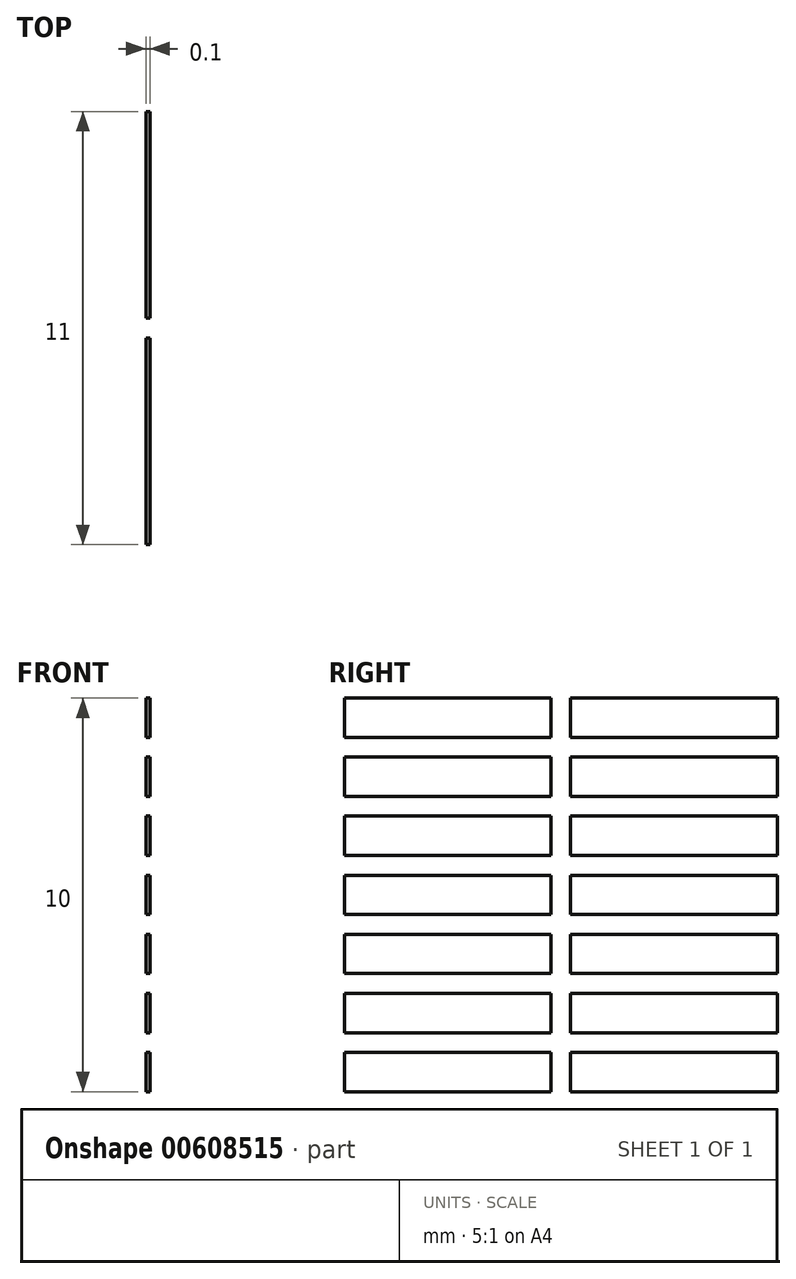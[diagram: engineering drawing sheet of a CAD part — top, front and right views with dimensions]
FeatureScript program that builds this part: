
annotation { "Feature Type Name" : "Feature", "Feature Type Description" : "" }
export const myFeature = defineFeature(function(context is Context, id is Id, definition is map)
    precondition{}
    {
        {
            var Q0;
            Q0=qCreatedBy(makeId("Right.planeOp"),FACE);
            var sketch = newSketch(context, id + "F0", { "sketchPlane" : qUnion([Q0])});
            skPoint(sketch, "E0.0", {"position": v(0, 0) * mm});
            skLineSegment(sketch, "E1.bottom", {"start": v(0, 0) * mm, "end": v(11.5, 0) * mm});
            skLineSegment(sketch, "E1.top", {"start": v(0, -11.5) * mm, "end": v(11.5, -11.5) * mm});
            skLineSegment(sketch, "E1.left", {"start": v(0, 0) * mm, "end": v(0, -11.5) * mm});
            skLineSegment(sketch, "E1.right", {"start": v(11.5, 0) * mm, "end": v(11.5, -11.5) * mm});
            skLineSegment(sketch, "E2.0", {"start": v(11.25, -0.25) * mm, "end": v(11.25, -1.25) * mm});
            skLineSegment(sketch, "E2.1", {"start": v(0.25, -0.25) * mm, "end": v(5.5, -0.25) * mm});
            skLineSegment(sketch, "E2.2", {"start": v(0.25, -0.25) * mm, "end": v(0.25, -1.25) * mm});
            skLineSegment(sketch, "E3.0", {"start": v(0.25, -10.25) * mm, "end": v(5.5, -10.25) * mm});
            skLineSegment(sketch, "E4", {"start": v(0.25, -1.25) * mm, "end": v(5.5, -1.25) * mm});
            skLineSegment(sketch, "E5", {"start": v(5.5, -1.25) * mm, "end": v(5.5, -0.25) * mm});
            skLineSegment(sketch, "E6.0", {"start": v(0.25, -1.75) * mm, "end": v(5.5, -1.75) * mm});
            skLineSegment(sketch, "E7", {"start": v(5.5, -1.75) * mm, "end": v(5.5, -2.75) * mm});
            skLineSegment(sketch, "E8", {"start": v(5.5, -2.75) * mm, "end": v(0.25, -2.75) * mm});
            skLineSegment(sketch, "E9.0", {"start": v(5.5, -3.25) * mm, "end": v(0.25, -3.25) * mm});
            skLineSegment(sketch, "E10", {"start": v(5.5, -3.25) * mm, "end": v(5.5, -4.25) * mm});
            skLineSegment(sketch, "E11", {"start": v(5.5, -4.25) * mm, "end": v(0.25, -4.25) * mm});
            skLineSegment(sketch, "E12.0", {"start": v(5.5, -4.75) * mm, "end": v(0.25, -4.75) * mm});
            skLineSegment(sketch, "E13", {"start": v(5.5, -4.75) * mm, "end": v(5.5, -5.75) * mm});
            skLineSegment(sketch, "E14", {"start": v(5.5, -5.75) * mm, "end": v(0.25, -5.75) * mm});
            skLineSegment(sketch, "E15.0", {"start": v(5.5, -6.25) * mm, "end": v(0.25, -6.25) * mm});
            skLineSegment(sketch, "E16", {"start": v(5.5, -6.25) * mm, "end": v(5.5, -7.25) * mm});
            skLineSegment(sketch, "E17", {"start": v(5.5, -7.25) * mm, "end": v(0.25, -7.25) * mm});
            skLineSegment(sketch, "E18.0", {"start": v(5.5, -7.75) * mm, "end": v(0.25, -7.75) * mm});
            skLineSegment(sketch, "E19", {"start": v(5.5, -7.75) * mm, "end": v(5.5, -8.75) * mm});
            skLineSegment(sketch, "E20", {"start": v(5.5, -8.75) * mm, "end": v(0.25, -8.75) * mm});
            skLineSegment(sketch, "E21.0", {"start": v(5.5, -9.25) * mm, "end": v(0.25, -9.25) * mm});
            skLineSegment(sketch, "E22", {"start": v(5.5, -9.25) * mm, "end": v(5.5, -10.25) * mm});
            skPoint(sketch, "E23.MirrorP", {"position": v(11.5, 0) * mm});
            skLineSegment(sketch, "E24.MirrorCS", {"start": v(6, -9.25) * mm, "end": v(11.25, -9.25) * mm});
            skLineSegment(sketch, "E25.MirrorCS", {"start": v(6, -4.75) * mm, "end": v(6, -5.75) * mm});
            skLineSegment(sketch, "E26.MirrorCS", {"start": v(6, -7.25) * mm, "end": v(11.25, -7.25) * mm});
            skLineSegment(sketch, "E27.MirrorCS", {"start": v(6, -8.75) * mm, "end": v(11.25, -8.75) * mm});
            skLineSegment(sketch, "E28.MirrorCS", {"start": v(6, -5.75) * mm, "end": v(11.25, -5.75) * mm});
            skLineSegment(sketch, "E29.MirrorCS", {"start": v(6, -4.25) * mm, "end": v(11.25, -4.25) * mm});
            skLineSegment(sketch, "E30.MirrorCS", {"start": v(6, -6.25) * mm, "end": v(11.25, -6.25) * mm});
            skLineSegment(sketch, "E31.MirrorCS", {"start": v(6, -2.75) * mm, "end": v(11.25, -2.75) * mm});
            skLineSegment(sketch, "E32.MirrorCS", {"start": v(6, -3.25) * mm, "end": v(11.25, -3.25) * mm});
            skLineSegment(sketch, "E33.MirrorCS", {"start": v(6, -7.75) * mm, "end": v(11.25, -7.75) * mm});
            skLineSegment(sketch, "E34.MirrorCS", {"start": v(6, -9.25) * mm, "end": v(6, -10.25) * mm});
            skLineSegment(sketch, "E35.MirrorCS", {"start": v(6, -1.75) * mm, "end": v(6, -2.75) * mm});
            skLineSegment(sketch, "E36.MirrorCS", {"start": v(11.25, -1.75) * mm, "end": v(6, -1.75) * mm});
            skLineSegment(sketch, "E37.MirrorCS", {"start": v(6, -3.25) * mm, "end": v(6, -4.25) * mm});
            skLineSegment(sketch, "E38.MirrorCS", {"start": v(6, -1.25) * mm, "end": v(6, -0.25) * mm});
            skLineSegment(sketch, "E39.MirrorCS", {"start": v(11.25, -1.25) * mm, "end": v(6, -1.25) * mm});
            skLineSegment(sketch, "E40.MirrorCS", {"start": v(6, -7.75) * mm, "end": v(6, -8.75) * mm});
            skLineSegment(sketch, "E41.MirrorCS", {"start": v(6, -6.25) * mm, "end": v(6, -7.25) * mm});
            skLineSegment(sketch, "E42.MirrorCS", {"start": v(6, -4.75) * mm, "end": v(11.25, -4.75) * mm});
            skPoint(sketch, "E43.orphan", {"position": v(11.5, -10.25) * mm});
            skLineSegment(sketch, "E44.trimOffspring", {"start": v(6, -10.25) * mm, "end": v(11.25, -10.25) * mm});
            skPoint(sketch, "E45.orphan", {"position": v(0, -10.25) * mm});
            skLineSegment(sketch, "E46.trimOffspring", {"start": v(0.25, -9.25) * mm, "end": v(0.25, -10.25) * mm});
            skLineSegment(sketch, "E47.trimOffspring", {"start": v(11.25, -9.25) * mm, "end": v(11.25, -10.25) * mm});
            skLineSegment(sketch, "E48.trimOffspring", {"start": v(11.25, -7.75) * mm, "end": v(11.25, -8.75) * mm});
            skLineSegment(sketch, "E49.trimOffspring", {"start": v(0.25, -7.75) * mm, "end": v(0.25, -8.75) * mm});
            skLineSegment(sketch, "E50.trimOffspring", {"start": v(11.25, -6.25) * mm, "end": v(11.25, -7.25) * mm});
            skLineSegment(sketch, "E51.trimOffspring", {"start": v(11.25, -4.75) * mm, "end": v(11.25, -5.75) * mm});
            skLineSegment(sketch, "E52.trimOffspring", {"start": v(0.25, -6.25) * mm, "end": v(0.25, -7.25) * mm});
            skLineSegment(sketch, "E53.trimOffspring", {"start": v(0.25, -4.75) * mm, "end": v(0.25, -5.75) * mm});
            skLineSegment(sketch, "E54.trimOffspring", {"start": v(0.25, -3.25) * mm, "end": v(0.25, -4.25) * mm});
            skLineSegment(sketch, "E55.trimOffspring", {"start": v(0.25, -1.75) * mm, "end": v(0.25, -2.75) * mm});
            skLineSegment(sketch, "E56.trimOffspring", {"start": v(11.25, -3.25) * mm, "end": v(11.25, -4.25) * mm});
            skLineSegment(sketch, "E57.trimOffspring", {"start": v(11.25, -1.75) * mm, "end": v(11.25, -2.75) * mm});
            skLineSegment(sketch, "E58.trimOffspring", {"start": v(6, -0.25) * mm, "end": v(11.25, -0.25) * mm});
            skSolve(sketch);
        }
        {
            var Q0;
            Q0=makeQuery(id+"F0.imprint","IMPRINT",FACE,{"disambiguationData":[TD([[makeQuery(id+"F0.imprint","IMPRINT",EDGE,{"derivedFrom":sQuery(id+"F0.wireOp",EDGE,"E18.0")}),1.0]])]});
            var Q1;
            Q1=makeQuery(id+"F0.imprint","IMPRINT",FACE,{"disambiguationData":[TD([[makeQuery(id+"F0.imprint","IMPRINT",EDGE,{"derivedFrom":sQuery(id+"F0.wireOp",EDGE,"E3.0")}),1.0]])]});
            var Q2;
            Q2=makeQuery(id+"F0.imprint","IMPRINT",FACE,{"disambiguationData":[TD([[makeQuery(id+"F0.imprint","IMPRINT",EDGE,{"derivedFrom":sQuery(id+"F0.wireOp",EDGE,"E29.MirrorCS")}),1.0]])]});
            var Q3;
            Q3=makeQuery(id+"F0.imprint","IMPRINT",FACE,{"disambiguationData":[TD([[makeQuery(id+"F0.imprint","IMPRINT",EDGE,{"derivedFrom":sQuery(id+"F0.wireOp",EDGE,"E6.0")}),-1.0]])]});
            var Q4;
            Q4=makeQuery(id+"F0.imprint","IMPRINT",FACE,{"disambiguationData":[TD([[makeQuery(id+"F0.imprint","IMPRINT",EDGE,{"derivedFrom":sQuery(id+"F0.wireOp",EDGE,"E31.MirrorCS")}),1.0]])]});
            var Q5;
            Q5=makeQuery(id+"F0.imprint","IMPRINT",FACE,{"disambiguationData":[TD([[makeQuery(id+"F0.imprint","IMPRINT",EDGE,{"derivedFrom":sQuery(id+"F0.wireOp",EDGE,"E26.MirrorCS")}),1.0]])]});
            var Q6;
            Q6=makeQuery(id+"F0.imprint","IMPRINT",FACE,{"disambiguationData":[TD([[makeQuery(id+"F0.imprint","IMPRINT",EDGE,{"derivedFrom":sQuery(id+"F0.wireOp",EDGE,"E2.1")}),-1.0]])]});
            var Q7;
            Q7=makeQuery(id+"F0.imprint","IMPRINT",FACE,{"disambiguationData":[TD([[makeQuery(id+"F0.imprint","IMPRINT",EDGE,{"derivedFrom":sQuery(id+"F0.wireOp",EDGE,"E25.MirrorCS")}),1.0]])]});
            var Q8;
            Q8=makeQuery(id+"F0.imprint","IMPRINT",FACE,{"disambiguationData":[TD([[makeQuery(id+"F0.imprint","IMPRINT",EDGE,{"derivedFrom":sQuery(id+"F0.wireOp",EDGE,"E27.MirrorCS")}),1.0]])]});
            var Q9;
            Q9=makeQuery(id+"F0.imprint","IMPRINT",FACE,{"disambiguationData":[TD([[makeQuery(id+"F0.imprint","IMPRINT",EDGE,{"derivedFrom":sQuery(id+"F0.wireOp",EDGE,"E24.MirrorCS")}),-1.0]])]});
            var Q10;
            Q10=makeQuery(id+"F0.imprint","IMPRINT",FACE,{"disambiguationData":[TD([[makeQuery(id+"F0.imprint","IMPRINT",EDGE,{"derivedFrom":sQuery(id+"F0.wireOp",EDGE,"E12.0")}),1.0]])]});
            var Q11;
            Q11=makeQuery(id+"F0.imprint","IMPRINT",FACE,{"disambiguationData":[TD([[makeQuery(id+"F0.imprint","IMPRINT",EDGE,{"derivedFrom":sQuery(id+"F0.wireOp",EDGE,"E15.0")}),1.0]])]});
            var Q12;
            Q12=makeQuery(id+"F0.imprint","IMPRINT",FACE,{"disambiguationData":[TD([[makeQuery(id+"F0.imprint","IMPRINT",EDGE,{"derivedFrom":sQuery(id+"F0.wireOp",EDGE,"E9.0")}),1.0]])]});
            var Q13;
            Q13=makeQuery(id+"F0.imprint","IMPRINT",FACE,{"disambiguationData":[TD([[makeQuery(id+"F0.imprint","IMPRINT",EDGE,{"derivedFrom":sQuery(id+"F0.wireOp",EDGE,"E2.0")}),-1.0]])]});
            extrude(context, id + "F1", {"entities" : qUnion([Q0, Q1, Q2, Q3, Q4, Q5, Q6, Q7, Q8, Q9, Q10, Q11, Q12, Q13]), "depth" : .1 * mm, "offsetDistance" : 25 * mm});
        }
    });
